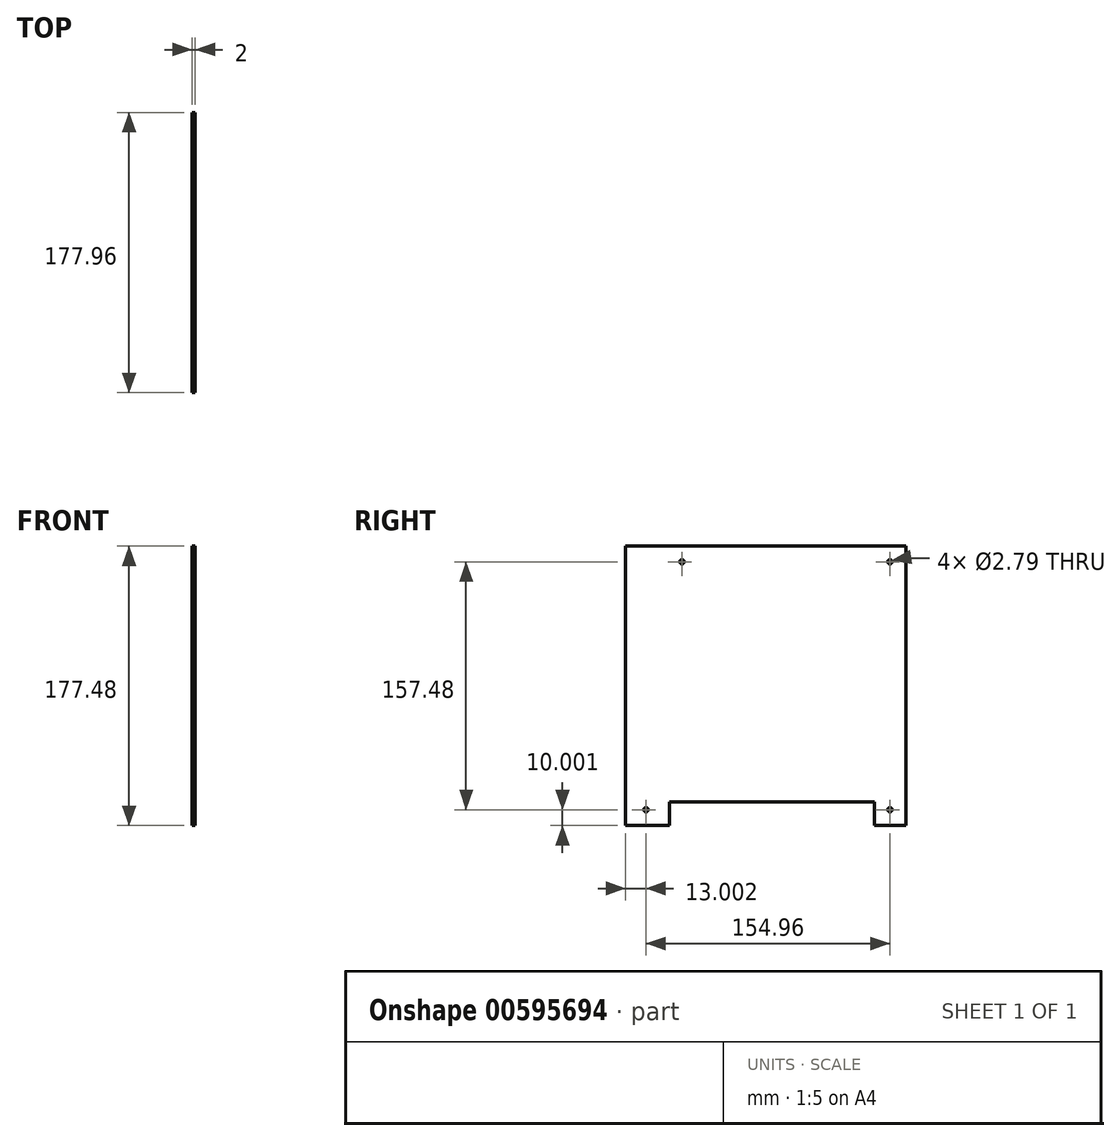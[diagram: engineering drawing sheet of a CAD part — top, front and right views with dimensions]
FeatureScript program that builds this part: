
annotation { "Feature Type Name" : "Feature", "Feature Type Description" : "" }
export const myFeature = defineFeature(function(context is Context, id is Id, definition is map)
    precondition{}
    {
        {
            var Q0;
            Q0=qCreatedBy(makeId("Right.planeOp"),FACE);
            var sketch = newSketch(context, id + "F0", { "sketchPlane" : qUnion([Q0])});
            skLineSegment(sketch, "E0.bottom", {"start": v(-83.68, 89.68) * mm, "end": v(94.28, 89.68) * mm});
            skLineSegment(sketch, "E0.top", {"start": v(-83.68, -87.8) * mm, "end": v(-55.72, -87.8) * mm});
            skLineSegment(sketch, "E0.left", {"start": v(-83.68, 89.68) * mm, "end": v(-83.68, -87.8) * mm});
            skLineSegment(sketch, "E0.right", {"start": v(94.28, 89.68) * mm, "end": v(94.28, -87.8) * mm});
            skCircle(sketch, "E1", {"center": v(-47.82, 79.68) * mm, "radius": 1.4 * mm});
            skCircle(sketch, "E2", {"center": v(84.28, 79.68) * mm, "radius": 1.4 * mm});
            skCircle(sketch, "E3", {"center": v(-70.68, -77.8) * mm, "radius": 1.4 * mm});
            skCircle(sketch, "E4", {"center": v(84.28, -77.8) * mm, "radius": 1.4 * mm});
            skLineSegment(sketch, "E5.top", {"start": v(-55.72, -72.8) * mm, "end": v(74.28, -72.8) * mm});
            skLineSegment(sketch, "E5.left", {"start": v(-55.72, -87.8) * mm, "end": v(-55.72, -72.8) * mm});
            skLineSegment(sketch, "E5.right", {"start": v(74.28, -87.8) * mm, "end": v(74.28, -72.8) * mm});
            skLineSegment(sketch, "E6.trimOffspring", {"start": v(74.28, -87.8) * mm, "end": v(94.28, -87.8) * mm});
            skSolve(sketch);
        }
        {
            var Q0;
            Q0 = qSketchRegion(id + "F0", true);
            extrude(context, id + "F1", {"entities" : qUnion([Q0]), "depth" : 2 * mm, "offsetDistance" : 25 * mm});
        }
    });
